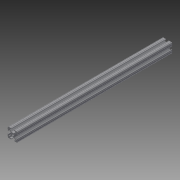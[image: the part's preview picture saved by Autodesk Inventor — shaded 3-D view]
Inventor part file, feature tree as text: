
AUTODESK INVENTOR PART (.ipt)
format: ipt  version: 2014 SP2 (Build 180246200, 246)  size: 197,120 bytes
history: native  units: in
note: dims shown in document units (in); Inventor stores cm internally (conversion verified against a paired STEP export)
features: other x21, extrude x1, sketch x1
ambient origin geometry x8: Origin, YZ Plane, XZ Plane, XY Plane, X Axis, Y Axis, Z Axis, Center Point
bodies: Solid1 (feature_tree)
feature tree (23):
  extrude  "Extrusion1"  [1 undecoded]
  other  "b1_XY"
  other  "b1_YZ"
  other  "b1_ZX"
  other  "b1_X"
  other  "b1_Y"
  other  "b1_Z"
  other  "b1_Center"
  other  "b2_XY"
  other  "b2_YZ"
  other  "b2_ZX"
  other  "b2_X"
  other  "b2_Y"
  other  "b2_Z"
  other  "b2_Center"
  other  "profile1010_XY"
  other  "profile1010_YZ"
  other  "profile1010_ZX"
  other  "profile1010_X"
  other  "profile1010_Y"
  other  "profile1010_Z"
  other  "profile1010_Center"
  sketch  "Sketch_1"  dims[d0=16.0in d1=0.0in]
note: 1 required parameter value undecoded (feature->parameter linkage not recoverable at this tier; creation-order binding heuristic only, values carry confidence <= 0.55)
